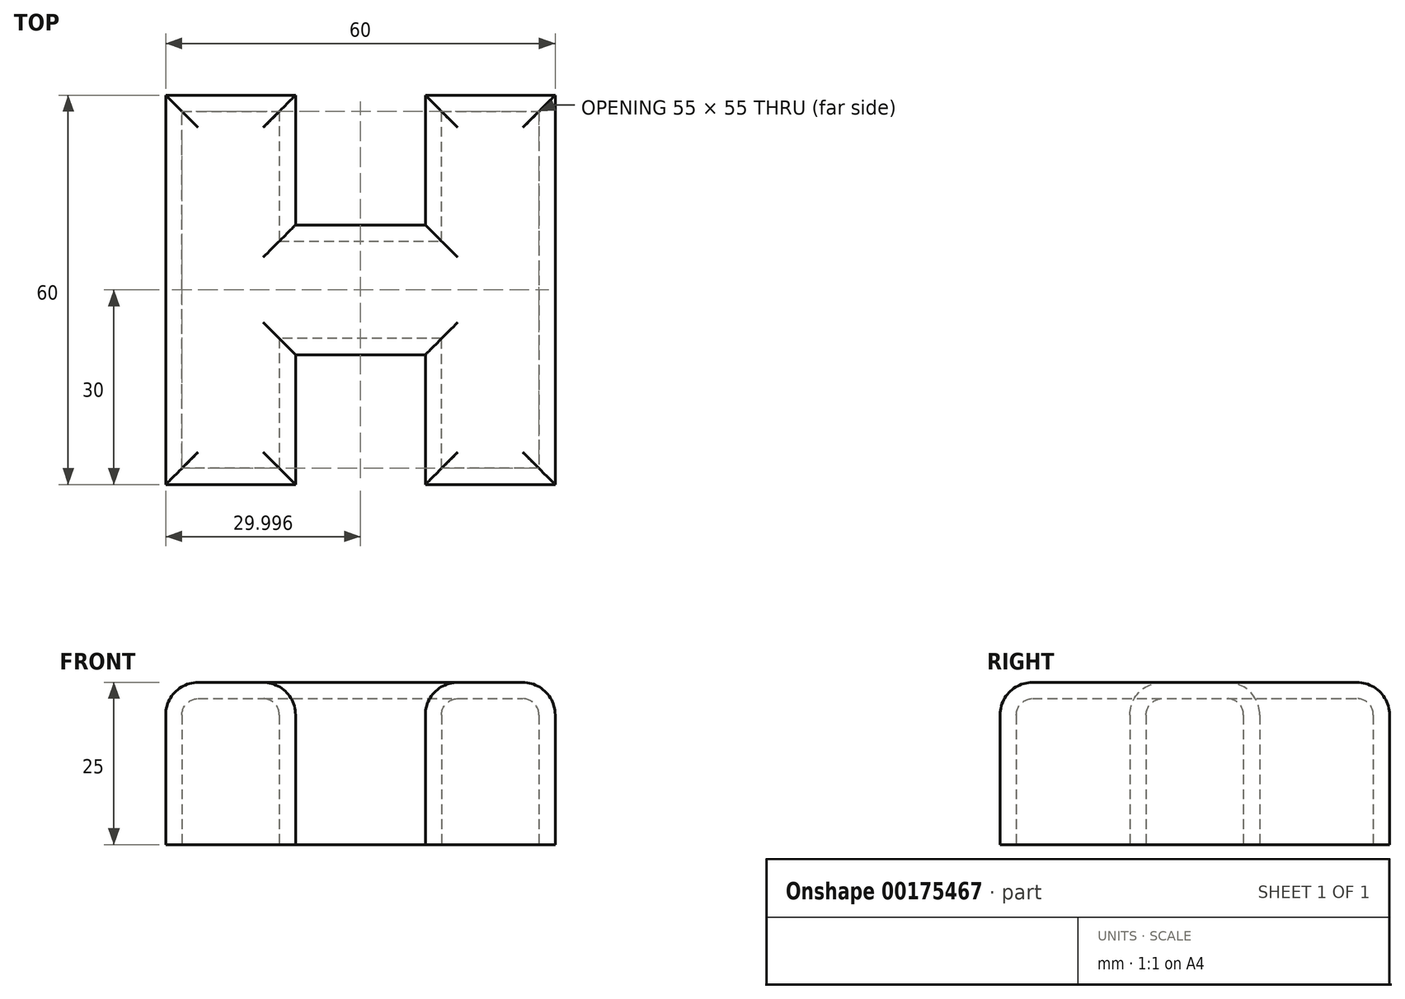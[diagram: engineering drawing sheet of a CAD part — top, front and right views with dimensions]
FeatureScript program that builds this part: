
annotation { "Feature Type Name" : "Feature", "Feature Type Description" : "" }
export const myFeature = defineFeature(function(context is Context, id is Id, definition is map)
    precondition{}
    {
        {
            var Q0;
            Q0=qCreatedBy(makeId("Top.planeOp"),FACE);
            var sketch = newSketch(context, id + "F0", { "sketchPlane" : qUnion([Q0])});
            skLineSegment(sketch, "E0", {"start": v(-42.33, 48.13) * mm, "end": v(-22.33, 48.13) * mm});
            skLineSegment(sketch, "E1", {"start": v(-22.33, 48.13) * mm, "end": v(-22.33, 28.13) * mm});
            skLineSegment(sketch, "E2", {"start": v(-22.33, 28.13) * mm, "end": v(-2.33, 28.13) * mm});
            skLineSegment(sketch, "E3", {"start": v(-2.33, 28.13) * mm, "end": v(-2.33, 48.13) * mm});
            skLineSegment(sketch, "E4", {"start": v(-2.33, 48.13) * mm, "end": v(17.67, 48.13) * mm});
            skLineSegment(sketch, "E5", {"start": v(17.67, 48.13) * mm, "end": v(17.67, -11.87) * mm});
            skLineSegment(sketch, "E6", {"start": v(17.67, -11.87) * mm, "end": v(-2.33, -11.87) * mm});
            skLineSegment(sketch, "E7", {"start": v(-2.33, -11.87) * mm, "end": v(-2.33, 8.13) * mm});
            skLineSegment(sketch, "E8", {"start": v(-2.33, 8.13) * mm, "end": v(-22.33, 8.13) * mm});
            skLineSegment(sketch, "E9", {"start": v(-22.33, 8.13) * mm, "end": v(-22.33, -11.87) * mm});
            skLineSegment(sketch, "E10", {"start": v(-22.33, -11.87) * mm, "end": v(-42.33, -11.87) * mm});
            skLineSegment(sketch, "E11", {"start": v(-42.33, -11.87) * mm, "end": v(-42.33, 48.13) * mm});
            skSolve(sketch);
        }
        {
            var Q0;
            Q0=makeQuery(id+"F0.imprint","IMPRINT",FACE,{"disambiguationData":[TD([[makeQuery(id+"F0.imprint","IMPRINT",EDGE,{"derivedFrom":sQuery(id+"F0.wireOp",EDGE,"E0")}),-1.0]])]});
            extrude(context, id + "F1", {"entities" : qUnion([Q0]), "depth" : 25 * mm});
        }
        {
            var Q0;
            Q0=makeQuery(id+"F1.opExtrude","CAP_EDGE",EDGE,{"disambiguationData":[OSD([sQuery(id+"F0.wireOp",EDGE,"E11")])],"isStart":false});
            var Q1;
            Q1=makeQuery(id+"F1.opExtrude","CAP_EDGE",EDGE,{"disambiguationData":[OSD([sQuery(id+"F0.wireOp",EDGE,"E10")])],"isStart":false});
            var Q2;
            Q2=makeQuery(id+"F1.opExtrude","CAP_EDGE",EDGE,{"disambiguationData":[OSD([sQuery(id+"F0.wireOp",EDGE,"E9")])],"isStart":false});
            var Q3;
            Q3=makeQuery(id+"F1.opExtrude","CAP_EDGE",EDGE,{"disambiguationData":[OSD([sQuery(id+"F0.wireOp",EDGE,"E8")])],"isStart":false});
            var Q4;
            Q4=makeQuery(id+"F1.opExtrude","CAP_EDGE",EDGE,{"disambiguationData":[OSD([sQuery(id+"F0.wireOp",EDGE,"E6")])],"isStart":false});
            var Q5;
            Q5=makeQuery(id+"F1.opExtrude","CAP_EDGE",EDGE,{"disambiguationData":[OSD([sQuery(id+"F0.wireOp",EDGE,"E5")])],"isStart":false});
            var Q6;
            Q6=makeQuery(id+"F1.opExtrude","CAP_EDGE",EDGE,{"disambiguationData":[OSD([sQuery(id+"F0.wireOp",EDGE,"E4")])],"isStart":false});
            var Q7;
            Q7=makeQuery(id+"F1.opExtrude","CAP_EDGE",EDGE,{"disambiguationData":[OSD([sQuery(id+"F0.wireOp",EDGE,"E3")])],"isStart":false});
            var Q8;
            Q8=makeQuery(id+"F1.opExtrude","CAP_EDGE",EDGE,{"disambiguationData":[OSD([sQuery(id+"F0.wireOp",EDGE,"E2")])],"isStart":false});
            var Q9;
            Q9=makeQuery(id+"F1.opExtrude","CAP_EDGE",EDGE,{"disambiguationData":[OSD([sQuery(id+"F0.wireOp",EDGE,"E1")])],"isStart":false});
            var Q10;
            Q10=makeQuery(id+"F1.opExtrude","CAP_EDGE",EDGE,{"disambiguationData":[OSD([sQuery(id+"F0.wireOp",EDGE,"E0")])],"isStart":false});
            var Q11;
            Q11=makeQuery(id+"F1.opExtrude","CAP_EDGE",EDGE,{"disambiguationData":[OSD([sQuery(id+"F0.wireOp",EDGE,"E7")])],"isStart":false});
            fillet(context, id + "F2", {"entities" : qUnion([Q0, Q1, Q2, Q3, Q4, Q5, Q6, Q7, Q8, Q9, Q10, Q11]), "radius" : 5 * mm, "tangentPropagation" : true, "allowEdgeOverflow" : false});
        }
        {
            var Q0;
            Q0=makeQuery(id+"F1.opExtrude","CAP_FACE",FACE,{"disambiguationData":[OSD([sQuery(id+"F0.wireOp",EDGE,"E0"),sQuery(id+"F0.wireOp",EDGE,"E1"),sQuery(id+"F0.wireOp",EDGE,"E2"),sQuery(id+"F0.wireOp",EDGE,"E3"),sQuery(id+"F0.wireOp",EDGE,"E4"),sQuery(id+"F0.wireOp",EDGE,"E5"),sQuery(id+"F0.wireOp",EDGE,"E6"),sQuery(id+"F0.wireOp",EDGE,"E7"),sQuery(id+"F0.wireOp",EDGE,"E8"),sQuery(id+"F0.wireOp",EDGE,"E9"),sQuery(id+"F0.wireOp",EDGE,"E10"),sQuery(id+"F0.wireOp",EDGE,"E11")])],"isStart":true});
            shell(context, id + "F3", {"entities" : qUnion([Q0]), "thickness" : 2.5 * mm});
        }
    });
